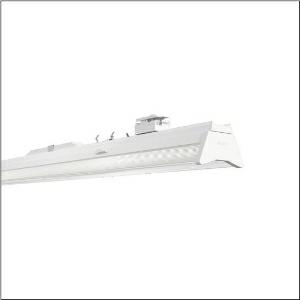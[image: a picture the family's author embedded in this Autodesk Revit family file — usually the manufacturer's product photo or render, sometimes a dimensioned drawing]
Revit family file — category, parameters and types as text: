
# Revit family: licross_21_performance_mo_51td16vnd45g
name_source: partatom
category: Lighting Fixtures
units: mm (PartAtom-declared; Revit-internal decimal feet)

## family parameters
Cut with Voids When Loaded = No
Host = Face
Light Source = No
Part Type = Normal
Room Calculation Point = No
Round Connector Dimension = Use Diameter
Shared = No

## types (1)
- --- (1 x LED, 4500 lm, 26.3 W, 4000K)
    Apparent Load = 26 VA
    CIE Flux Codes = 66 88 96 79 100
    Color Rendering = 90
    Color Temperature = 4000K
    Default Elevation = 1800 mm
    Description = Licross 21 Performance MO, luminaire insert, of sheet steel, galvanised, coil coated, white, length: 1.500mm, width: 120mm, height: 123mm, LED rated luminous flux: 4.500lm, light colour: 940, SDCM (Standard Deviation of Colour Matching)MacAdam ≤ 2 SDCM (initial), control gear: DALI 2, CLO, with plug, 5-pole, with phase selection, mains connection: 220..240V, AC, 50/60Hz, start of lifetime: 26W, end of service life: 29W, internal wiring halogen-free, primary light control with lens, of plastic, primary optical cover: cover, of PMMA, light emission: direct/indirect distribution, primary light characteristic: symmetric, protection rating (complete): IP54, insulation class (complete): insulation class I (protective earthing), certification: CE, ENEC, VDE, UKCA, protection symbol: D if used in an environment with non-conductive dust loads with corresponding accessories, impact resistance: IK06, permissible ambient temperature for indoor applications: -25..+45°C, corresponds to IFS (International Featured Standards) requirements for safety and quality in the food industry, reducing of maximum allowable ambient temperature of 5°C with ceiling mounting, LABS conformity tested according to VDMA 24364:2018-05, The light source and the operating device comply with the requirements of the Ecodesign Regulation (EU) 2019/2020 and are replaceable in accordance with this regulation, packaging unit: 1 piece
    Height = 114 mm
    Lamp = 1 x LED
    Lamp Light Flux = 4500 lm
    Lamp Power = 26.3 W
    Lamp count = 1
    Length = 1500 mm
    Luminous efficacy = 171 lm/W
    Manufacturer = Siteco
    ModVariant = No
    Model = 51TD16VND45G
    Mounting Place = Ceiling
    Mounting Type = Pendant
    Number of Poles = 1
    OnlyDefault = Yes
    Power Factor = 1
    Product Name = Licross 21 Performance MO
    Product group = luminaire insert | ceiling pendant
    ProductGroupID = 901
    Protection Class = Protection class I
    Protection Degree = IP 54
    RLX_Detail_Level = 1
    RLX_Emergency_Light_Flux = 0 lm
    RLX_Emergency_Type = 0
    RLX_Emergency_Type_DB = No
    RlxData = <blob elided: 34105 chars, md5=e7c17f8f>
    Socket = socket
    Standby Power = 0 W
    System Light Flux = 4500 lm
    System Power = 26 W
    Type Comments = factory setting: luminous flux: 100 % | dim-lin: 254 | 174 mA
    Type Image = l_1256138.jpg
    URL = http://relux.com
    VarID = @adj_056465
    Voltage = 0 V
    Weight = 0.00 kg
    Width = 120 mm

## geometry (parser evidence)
native form markers: Blend x4, Sweep x12
no freeform markers — native parametric forms only
